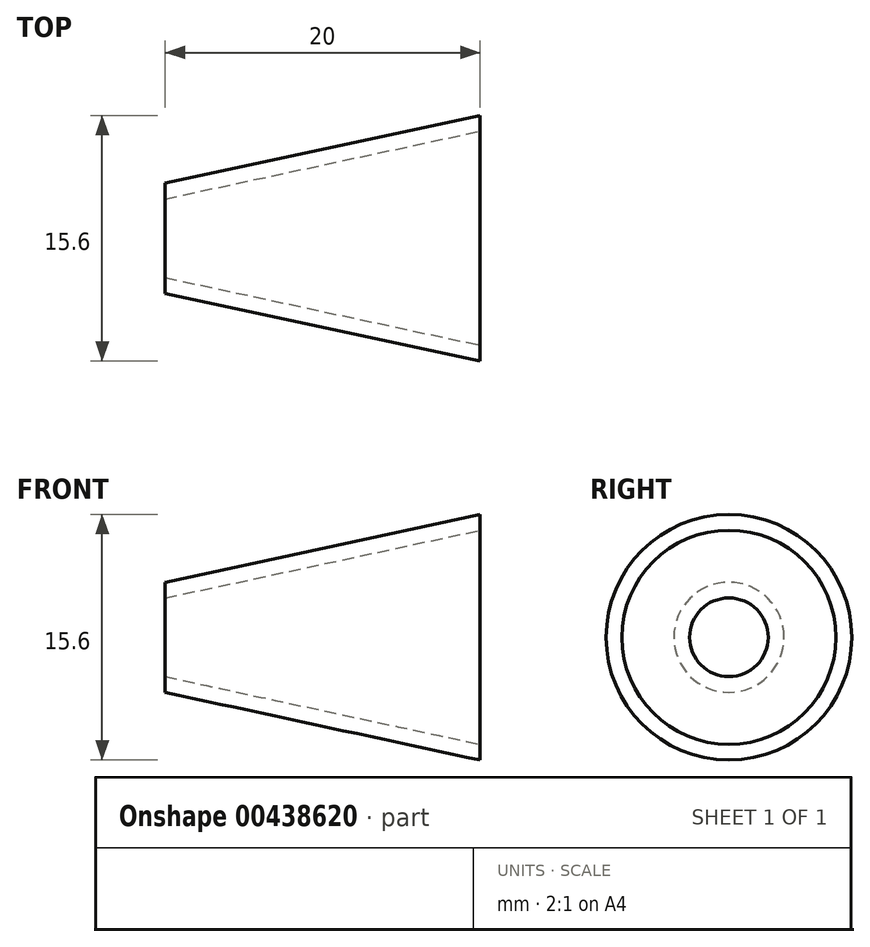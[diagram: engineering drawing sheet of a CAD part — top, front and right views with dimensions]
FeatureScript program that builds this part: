
annotation { "Feature Type Name" : "Feature", "Feature Type Description" : "" }
export const myFeature = defineFeature(function(context is Context, id is Id, definition is map)
    precondition{}
    {
        {
            var Q0;
            Q0=qCreatedBy(makeId("Right.planeOp"),FACE);
            cPlane(context, id + "F0", {"entities" : qUnion([Q0]), "cplaneType" : CPlaneType.OFFSET, "offset" : 20 * mm, "width" : 150 * mm, "height" : 150 * mm});
        }
        {
            var Q0;
            Q0=qCreatedBy(makeId("Right.planeOp"),FACE);
            var sketch = newSketch(context, id + "F1", { "sketchPlane" : qUnion([Q0])});
            skCircle(sketch, "E0", {"center": v(0, 0) * mm, "radius": 3.5 * mm});
            skSolve(sketch);
        }
        {
            var Q0;
            Q0=qCreatedBy(id+"F0.planeOp",FACE);
            var sketch = newSketch(context, id + "F2", { "sketchPlane" : qUnion([Q0])});
            skCircle(sketch, "E1", {"center": v(0, 0) * mm, "radius": 7.8 * mm});
            skSolve(sketch);
        }
        {
            var Q0;
            Q0=makeQuery(id+"F2.imprint","IMPRINT",FACE,{"disambiguationData":[TD([[makeQuery(id+"F2.imprint","IMPRINT",EDGE,{"derivedFrom":sQuery(id+"F2.wireOp",EDGE,"E1")}),1.0]])]});
            var Q1;
            Q1=makeQuery(id+"F1.imprint","IMPRINT",FACE,{"disambiguationData":[TD([[makeQuery(id+"F1.imprint","IMPRINT",EDGE,{"derivedFrom":sQuery(id+"F1.wireOp",EDGE,"E0")}),1.0]])]});
            loft(context, id + "F3", {"sheetProfilesArray" : [{ "sheetProfileEntities" : qUnion([Q0]) }, { "sheetProfileEntities" : qUnion([Q1]) }]});
        }
        {
            var Q0;
            Q0=makeQuery(id+"F3.opLoft","CAP_FACE",FACE,{"disambiguationData":[OSD([makeQuery(id+"F1.imprint","IMPRINT",FACE,{"disambiguationData":[TD([[makeQuery(id+"F1.imprint","IMPRINT",EDGE,{"derivedFrom":sQuery(id+"F1.wireOp",EDGE,"E0")}),1.0]])]})])],"isStart":true});
            var sketch = newSketch(context, id + "F4", { "sketchPlane" : qUnion([Q0])});
            skCircle(sketch, "E2", {"center": v(0, 0) * mm, "radius": 2.5 * mm});
            skSolve(sketch);
        }
        {
            var Q0;
            Q0=makeQuery(id+"F3.opLoft","CAP_FACE",FACE,{"disambiguationData":[OSD([makeQuery(id+"F2.imprint","IMPRINT",FACE,{"disambiguationData":[TD([[makeQuery(id+"F2.imprint","IMPRINT",EDGE,{"derivedFrom":sQuery(id+"F2.wireOp",EDGE,"E1")}),1.0]])]})])],"isStart":true});
            var sketch = newSketch(context, id + "F5", { "sketchPlane" : qUnion([Q0])});
            skCircle(sketch, "E3", {"center": v(0, 0) * mm, "radius": 6.8 * mm});
            skSolve(sketch);
        }
        {
            var Q1;
            Q1=makeQuery(id+"F5.imprint","IMPRINT",FACE,{"disambiguationData":[TD([[makeQuery(id+"F5.imprint","IMPRINT",EDGE,{"derivedFrom":sQuery(id+"F5.wireOp",EDGE,"E3")}),1.0]])]});
            var Q2;
            Q2=makeQuery(id+"F4.imprint","IMPRINT",FACE,{"disambiguationData":[TD([[makeQuery(id+"F4.imprint","IMPRINT",EDGE,{"derivedFrom":sQuery(id+"F4.wireOp",EDGE,"E2")}),1.0]])]});
            loft(context, id + "F6", {"operationType" : NewBodyOperationType.REMOVE, "sheetProfilesArray" : [{ "sheetProfileEntities" : qUnion([Q1]) }, { "sheetProfileEntities" : qUnion([Q2]) }]});
        }
    });
